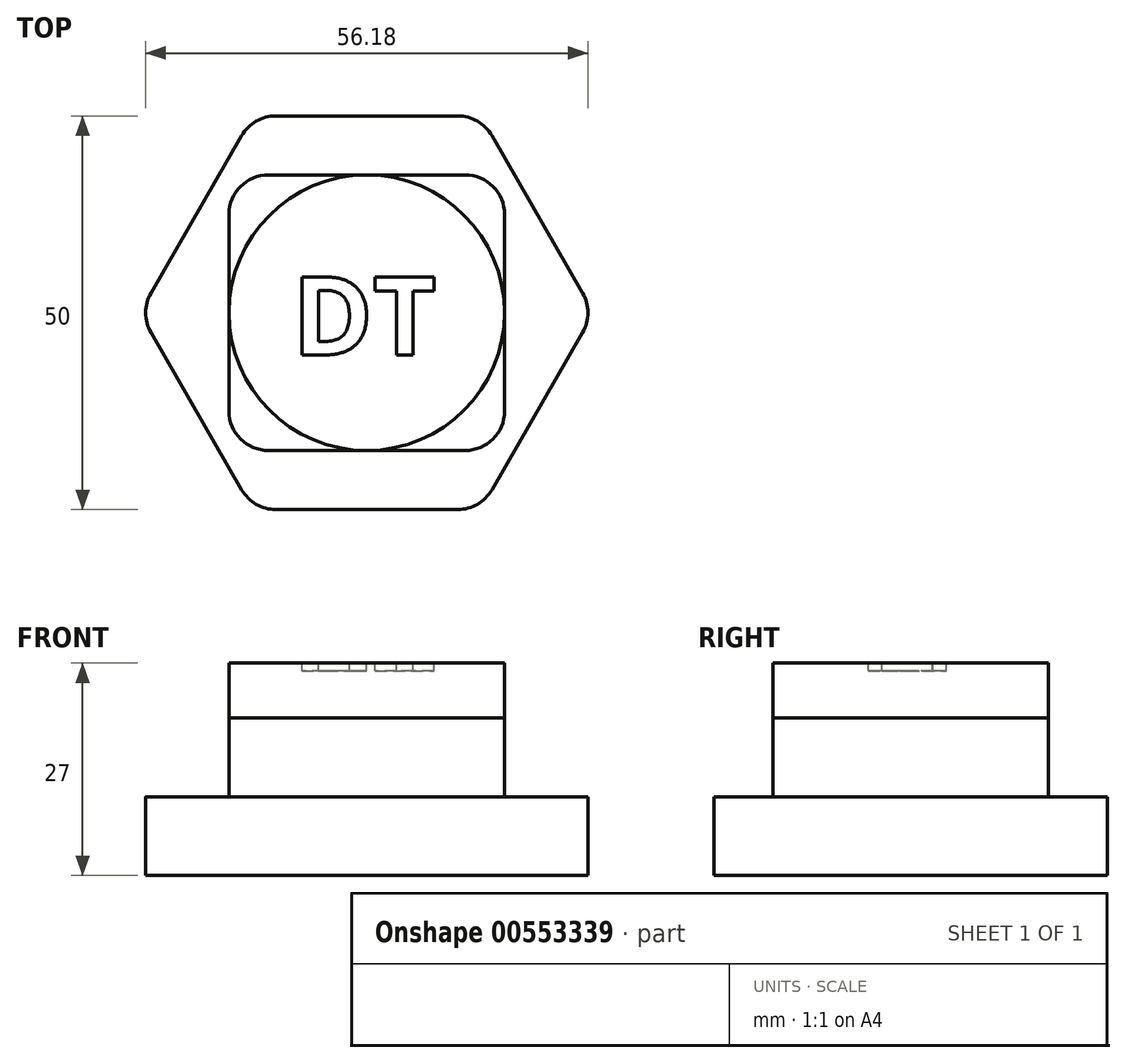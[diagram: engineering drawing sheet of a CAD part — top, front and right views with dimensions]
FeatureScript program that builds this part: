
annotation { "Feature Type Name" : "Feature", "Feature Type Description" : "" }
export const myFeature = defineFeature(function(context is Context, id is Id, definition is map)
    precondition{}
    {
        {
            var Q0;
            Q0=qCreatedBy(makeId("Top.planeOp"),FACE);
            var sketch = newSketch(context, id + "F0", { "sketchPlane" : qUnion([Q0])});
            skCircle(sketch, "E0.cCircle", {"center": v(0, 0) * mm, "radius": 25 * mm, "construction": true});
            skLineSegment(sketch, "E0.0", {"start": v(-14.43, 25) * mm, "end": v(14.43, 25) * mm});
            skLineSegment(sketch, "E0.1", {"start": v(14.43, 25) * mm, "end": v(28.87, 0) * mm});
            skLineSegment(sketch, "E0.2", {"start": v(28.87, 0) * mm, "end": v(14.43, -25) * mm});
            skLineSegment(sketch, "E0.3", {"start": v(14.43, -25) * mm, "end": v(-14.43, -25) * mm});
            skLineSegment(sketch, "E0.4", {"start": v(-14.43, -25) * mm, "end": v(-28.87, 0) * mm});
            skLineSegment(sketch, "E0.5", {"start": v(-28.87, 0) * mm, "end": v(-14.43, 25) * mm});
            skPoint(sketch, "E0.0.midPoint", {"position": v(0, 25) * mm});
            skSolve(sketch);
        }
        {
            var Q0;
            Q0=makeQuery(id+"F0.imprint","IMPRINT",FACE,{"disambiguationData":[TD([[makeQuery(id+"F0.imprint","IMPRINT",EDGE,{"derivedFrom":sQuery(id+"F0.wireOp",EDGE,"E0.0")}),-1.0]])]});
            extrude(context, id + "F1", {"entities" : qUnion([Q0]), "depth" : 10 * mm, "offsetDistance" : 25 * mm});
        }
        {
            var Q0;
            Q0=makeQuery(id+"F1.opExtrude","CAP_FACE",FACE,{"disambiguationData":[OSD([sQuery(id+"F0.wireOp",EDGE,"E0.0"),sQuery(id+"F0.wireOp",EDGE,"E0.1"),sQuery(id+"F0.wireOp",EDGE,"E0.2"),sQuery(id+"F0.wireOp",EDGE,"E0.3"),sQuery(id+"F0.wireOp",EDGE,"E0.4"),sQuery(id+"F0.wireOp",EDGE,"E0.5")])],"isStart":false});
            var sketch = newSketch(context, id + "F2", { "sketchPlane" : qUnion([Q0])});
            skLineSegment(sketch, "E1.bottom", {"start": v(-17.5, 17.5) * mm, "end": v(17.5, 17.5) * mm});
            skLineSegment(sketch, "E1.top", {"start": v(-17.5, -17.5) * mm, "end": v(17.5, -17.5) * mm});
            skLineSegment(sketch, "E1.left", {"start": v(-17.5, 17.5) * mm, "end": v(-17.5, -17.5) * mm});
            skLineSegment(sketch, "E1.right", {"start": v(17.5, 17.5) * mm, "end": v(17.5, -17.5) * mm});
            skPoint(sketch, "E1.middle", {"position": v(0, 0) * mm});
            skSolve(sketch);
        }
        {
            var Q0;
            Q0=qSketchRegion(id+"F2",true);
            extrude(context, id + "F3", {"entities" : qUnion([Q0]), "operationType" : NewBodyOperationType.ADD, "depth" : 10 * mm, "offsetDistance" : 25 * mm});
        }
        {
            var Q0;
            Q0=makeQuery(id+"F1.opExtrude","SWEPT_EDGE",EDGE,{"disambiguationData":[OSD([sQuery(id+"F0.wireOp",EDGE,"E0.4"),sQuery(id+"F0.wireOp",EDGE,"E0.5")])]});
            var Q1;
            Q1=makeQuery(id+"F1.opExtrude","SWEPT_EDGE",EDGE,{"disambiguationData":[OSD([sQuery(id+"F0.wireOp",EDGE,"E0.3"),sQuery(id+"F0.wireOp",EDGE,"E0.4")])]});
            var Q2;
            Q2=makeQuery(id+"F1.opExtrude","SWEPT_EDGE",EDGE,{"disambiguationData":[OSD([sQuery(id+"F0.wireOp",EDGE,"E0.2"),sQuery(id+"F0.wireOp",EDGE,"E0.3")])]});
            var Q3;
            Q3=makeQuery(id+"F1.opExtrude","SWEPT_EDGE",EDGE,{"disambiguationData":[OSD([sQuery(id+"F0.wireOp",EDGE,"E0.1"),sQuery(id+"F0.wireOp",EDGE,"E0.2")])]});
            var Q4;
            Q4=makeQuery(id+"F1.opExtrude","SWEPT_EDGE",EDGE,{"disambiguationData":[OSD([sQuery(id+"F0.wireOp",EDGE,"E0.0"),sQuery(id+"F0.wireOp",EDGE,"E0.1")])]});
            var Q5;
            Q5=makeQuery(id+"F1.opExtrude","SWEPT_EDGE",EDGE,{"disambiguationData":[OSD([sQuery(id+"F0.wireOp",EDGE,"E0.0"),sQuery(id+"F0.wireOp",EDGE,"E0.5")])]});
            var Q6;
            Q6=makeQuery(id+"F3.opExtrude","SWEPT_EDGE",EDGE,{"disambiguationData":[OSD([sQuery(id+"F2.wireOp",EDGE,"E1.bottom"),sQuery(id+"F2.wireOp",EDGE,"E1.left")])]});
            var Q7;
            Q7=makeQuery(id+"F3.opExtrude","SWEPT_EDGE",EDGE,{"disambiguationData":[OSD([sQuery(id+"F2.wireOp",EDGE,"E1.top"),sQuery(id+"F2.wireOp",EDGE,"E1.left")])]});
            var Q8;
            Q8=makeQuery(id+"F3.opExtrude","SWEPT_EDGE",EDGE,{"disambiguationData":[OSD([sQuery(id+"F2.wireOp",EDGE,"E1.top"),sQuery(id+"F2.wireOp",EDGE,"E1.right")])]});
            var Q9;
            Q9=makeQuery(id+"F3.opExtrude","SWEPT_EDGE",EDGE,{"disambiguationData":[OSD([sQuery(id+"F2.wireOp",EDGE,"E1.bottom"),sQuery(id+"F2.wireOp",EDGE,"E1.right")])]});
            fillet(context, id + "F4", {"entities" : qUnion([Q0, Q1, Q2, Q3, Q4, Q5, Q6, Q7, Q8, Q9]), "radius" : 5 * mm, "tangentPropagation" : true, "allowEdgeOverflow" : false});
        }
        {
            var Q0;
            Q0=makeQuery(id+"F3.opExtrude","CAP_FACE",FACE,{"disambiguationData":[OSD([sQuery(id+"F2.wireOp",EDGE,"E1.bottom"),sQuery(id+"F2.wireOp",EDGE,"E1.top"),sQuery(id+"F2.wireOp",EDGE,"E1.left"),sQuery(id+"F2.wireOp",EDGE,"E1.right")])],"isStart":false});
            var sketch = newSketch(context, id + "F5", { "sketchPlane" : qUnion([Q0])});
            skCircle(sketch, "E2", {"center": v(0, 0) * mm, "radius": 17.5 * mm});
            skSolve(sketch);
        }
        {
            var Q0;
            Q0=qSketchRegion(id+"F5",true);
            var Q1;
            Q1=sQuery(id+"F5.wireOp",EDGE,"E2");
            extrude(context, id + "F6", {"entities" : qUnion([Q0]), "surfaceEntities" : qUnion([Q1]), "depth" : 7 * mm, "offsetDistance" : 25 * mm});
        }
        {
            var Q0;
            Q0=makeQuery(id+"F6.opExtrude","CAP_FACE",FACE,{"disambiguationData":[OSD([sQuery(id+"F5.wireOp",EDGE,"E2")])],"isStart":false});
            var sketch = newSketch(context, id + "F7", { "sketchPlane" : qUnion([Q0])});
            skText(sketch, "E3", { "text": "DT", "fontName": "OpenSans-Bold.ttf"});
            const initialGuessF7  = {"E3": [-0.0095, -0.00538, 1, 0, 0.01]};
            skSetInitialGuess(sketch, initialGuessF7);
            skSolve(sketch);
        }
        {
            var Q0;
            Q0=qSketchRegion(id+"F7",true);
            extrude(context, id + "F8", {"entities" : qUnion([Q0]), "operationType" : NewBodyOperationType.REMOVE, "oppositeDirection" : true, "depth" : 1 * mm, "offsetDistance" : 25 * mm});
        }
    });
